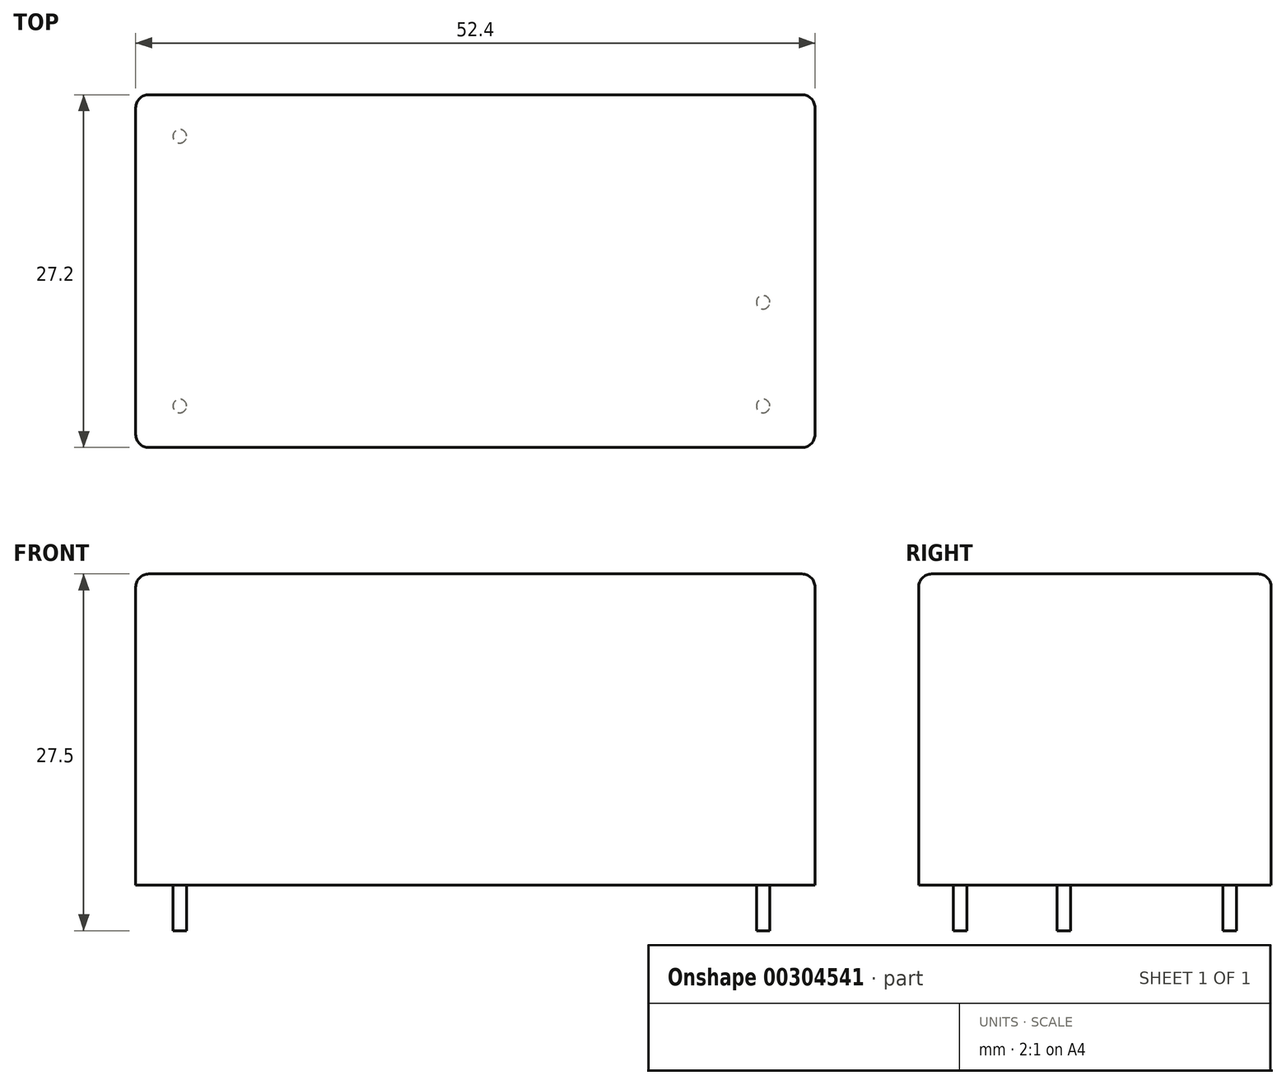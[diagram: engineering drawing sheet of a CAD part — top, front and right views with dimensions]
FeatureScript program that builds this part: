
annotation { "Feature Type Name" : "Feature", "Feature Type Description" : "" }
export const myFeature = defineFeature(function(context is Context, id is Id, definition is map)
    precondition{}
    {
        {
            var Q0;
            Q0=qCreatedBy(makeId("Top.planeOp"),FACE);
            var sketch = newSketch(context, id + "F0", { "sketchPlane" : qUnion([Q0])});
            skLineSegment(sketch, "E0.bottom", {"start": v(0, 0) * mm, "end": v(52.4, 0) * mm});
            skLineSegment(sketch, "E0.top", {"start": v(0, 27.2) * mm, "end": v(52.4, 27.2) * mm});
            skLineSegment(sketch, "E0.left", {"start": v(0, 0) * mm, "end": v(0, 27.2) * mm});
            skLineSegment(sketch, "E0.right", {"start": v(52.4, 0) * mm, "end": v(52.4, 27.2) * mm});
            skSolve(sketch);
        }
        {
            var Q0;
            Q0 = qSketchRegion(id + "F0", true);
            extrude(context, id + "F1", {"entities" : qUnion([Q0]), "depth" : 24 * mm});
        }
        {
            var Q0;
            Q0=qCreatedBy(makeId("Top.planeOp"),FACE);
            var sketch = newSketch(context, id + "F2", { "sketchPlane" : qUnion([Q0])});
            skCircle(sketch, "E1", {"center": v(3.4, 3.2) * mm, "radius": 0.52 * mm});
            skCircle(sketch, "E2", {"center": v(3.4, 24) * mm, "radius": 0.52 * mm});
            skCircle(sketch, "E3", {"center": v(48.4, 3.2) * mm, "radius": 0.52 * mm});
            skCircle(sketch, "E4", {"center": v(48.4, 11.2) * mm, "radius": 0.52 * mm});
            skLineSegment(sketch, "E5", {"start": v(3.4, 3.2) * mm, "end": v(3.4, 24) * mm, "construction": true});
            skLineSegment(sketch, "E6", {"start": v(48.4, 3.2) * mm, "end": v(48.4, 11.2) * mm, "construction": true});
            skLineSegment(sketch, "E7", {"start": v(3.4, 3.2) * mm, "end": v(48.4, 3.2) * mm, "construction": true});
            skSolve(sketch);
        }
        {
            var Q0;
            Q0 = qSketchRegion(id + "F2", true);
            extrude(context, id + "F3", {"entities" : qUnion([Q0]), "operationType" : NewBodyOperationType.ADD, "oppositeDirection" : true, "depth" : 3.5 * mm});
        }
        {
            var Q0;
            Q0=makeQuery(id+"F1.opExtrude","SWEPT_EDGE",EDGE,{"disambiguationData":[OSD([sQuery(id+"F0.wireOp",EDGE,"E0.bottom"),sQuery(id+"F0.wireOp",EDGE,"E0.left")])]});
            var Q1;
            Q1=makeQuery(id+"F1.opExtrude","SWEPT_EDGE",EDGE,{"disambiguationData":[OSD([sQuery(id+"F0.wireOp",EDGE,"E0.bottom"),sQuery(id+"F0.wireOp",EDGE,"E0.right")])]});
            var Q2;
            Q2=makeQuery(id+"F1.opExtrude","SWEPT_EDGE",EDGE,{"disambiguationData":[OSD([sQuery(id+"F0.wireOp",EDGE,"E0.top"),sQuery(id+"F0.wireOp",EDGE,"E0.left")])]});
            var Q3;
            Q3=makeQuery(id+"F1.opExtrude","CAP_EDGE",EDGE,{"disambiguationData":[OSD([sQuery(id+"F0.wireOp",EDGE,"E0.left")])],"isStart":false});
            var Q4;
            Q4=makeQuery(id+"F1.opExtrude","CAP_EDGE",EDGE,{"disambiguationData":[OSD([sQuery(id+"F0.wireOp",EDGE,"E0.top")])],"isStart":false});
            var Q5;
            Q5=makeQuery(id+"F1.opExtrude","SWEPT_EDGE",EDGE,{"disambiguationData":[OSD([sQuery(id+"F0.wireOp",EDGE,"E0.top"),sQuery(id+"F0.wireOp",EDGE,"E0.right")])]});
            var Q6;
            Q6=makeQuery(id+"F1.opExtrude","CAP_EDGE",EDGE,{"disambiguationData":[OSD([sQuery(id+"F0.wireOp",EDGE,"E0.right")])],"isStart":false});
            var Q7;
            Q7=makeQuery(id+"F1.opExtrude","CAP_EDGE",EDGE,{"disambiguationData":[OSD([sQuery(id+"F0.wireOp",EDGE,"E0.bottom")])],"isStart":false});
            fillet(context, id + "F4", {"entities" : qUnion([Q0, Q1, Q2, Q3, Q4, Q5, Q6, Q7]), "radius" : 1 * mm, "tangentPropagation" : true, "allowEdgeOverflow" : false});
        }
    });
